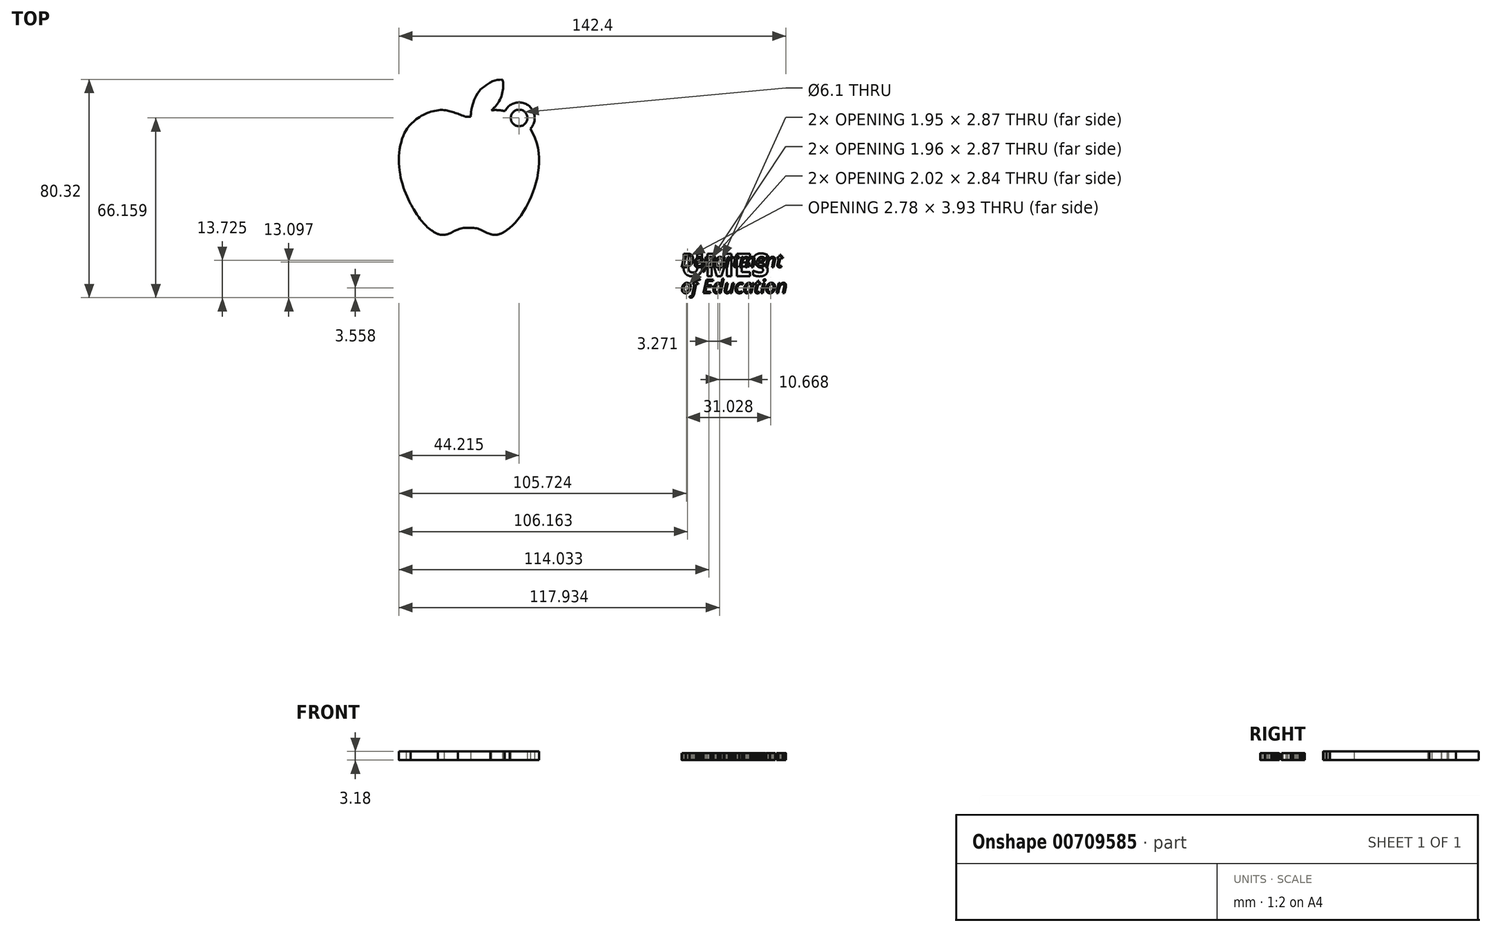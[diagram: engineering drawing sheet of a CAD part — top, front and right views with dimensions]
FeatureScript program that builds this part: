
annotation { "Feature Type Name" : "Feature", "Feature Type Description" : "" }
export const myFeature = defineFeature(function(context is Context, id is Id, definition is map)
    precondition{}
    {
        {
            var Q0;
            Q0=qCreatedBy(makeId("Top.planeOp"),FACE);
            var sketch = newSketch(context, id + "F0", { "sketchPlane" : qUnion([Q0])});
            skCircle(sketch, "E0", {"center": v(-59.53, 49.89) * mm, "radius": 3.05 * mm});
            skArc(sketch, "E1", {"start": v(-55.39, 45.93) * mm, "mid": v(-56.24, 54.59) * mm, "end": v(-64.67, 52.43) * mm});
            skFitSpline(sketch, "E2", {"points": [v(-64.67, 52.43) * mm, v(-69.66, 52.66) * mm, v(-71.93, 51.25) * mm], "startDerivative": vector(-9.59, 1.47) * mm, "endDerivative": vector(-4.68, -4.12) * mm});
            skFitSpline(sketch, "E3", {"points": [v(-69.66, 52.66) * mm, v(-66.9, 56.02) * mm, v(-65.54, 59.96) * mm, v(-65.4, 62.82) * mm, v(-65.72, 64.05) * mm], "startDerivative": vector(10.2, 10.54) * mm, "endDerivative": vector(-2.35, 6.78) * mm});
            skFitSpline(sketch, "E4", {"points": [v(-65.72, 64.05) * mm, v(-68.98, 63.5) * mm, v(-71.84, 61.82) * mm, v(-74.02, 60) * mm, v(-75.65, 57.33) * mm, v(-76.7, 54.52) * mm, v(-77.24, 51.57) * mm, v(-77.33, 50.3) * mm], "startDerivative": vector(-21.52, -1.58) * mm, "endDerivative": vector(-0.5, -11.65) * mm});
            skFitSpline(sketch, "E5", {"points": [v(-55.39, 45.93) * mm, v(-53.32, 41.64) * mm, v(-52.33, 36.83) * mm, v(-52.25, 32.55) * mm, v(-52.86, 27.98) * mm, v(-54.08, 23.47) * mm, v(-55.53, 19.81) * mm, v(-56.76, 17.52) * mm, v(-58.66, 14.32) * mm, v(-61.1, 11.26) * mm, v(-63.03, 9.37) * mm], "startDerivative": vector(20.95, -37.89) * mm, "endDerivative": vector(-22.74, -21.29) * mm});
            skFitSpline(sketch, "E6", {"points": [v(-77.33, 50.3) * mm, v(-78.34, 50.3) * mm, v(-79, 50.3) * mm, v(-80.29, 50.74) * mm, v(-82.2, 51.46) * mm, v(-84.15, 52.11) * mm, v(-86.09, 52.63) * mm, v(-87.15, 52.8) * mm], "startDerivative": vector(-8.93, 0.19) * mm, "endDerivative": vector(-7.8, 1.04) * mm});
            skFitSpline(sketch, "E7", {"points": [v(-101.1, 45.32) * mm, v(-100.2, 46.7) * mm, v(-99.27, 47.73) * mm, v(-98.15, 48.76) * mm, v(-96.8, 49.81) * mm, v(-95.2, 50.8) * mm, v(-93.47, 51.64) * mm, v(-91.57, 52.29) * mm, v(-90.06, 52.6) * mm, v(-88.52, 52.83) * mm, v(-87.15, 52.8) * mm], "startDerivative": vector(8.76, 14.5) * mm, "endDerivative": vector(14.81, -1) * mm});
            skFitSpline(sketch, "E8", {"points": [v(-101.1, 45.32) * mm, v(-101.75, 44.24) * mm, v(-102.36, 42.8) * mm, v(-102.82, 41.3) * mm, v(-103.27, 39.67) * mm, v(-103.54, 37.87) * mm, v(-103.73, 36.2) * mm, v(-103.73, 34.25) * mm, v(-103.73, 32.5) * mm, v(-103.52, 30.7) * mm, v(-103.21, 28.58) * mm, v(-102.83, 26.87) * mm, v(-102.4, 25.42) * mm, v(-102.07, 24.05) * mm, v(-101.5, 22.75) * mm, v(-100.84, 21.22) * mm, v(-100.41, 20.18) * mm, v(-100.06, 19.34) * mm, v(-99.47, 18.24) * mm], "startDerivative": vector(-13.27, -20.53) * mm, "endDerivative": vector(12.8, -22.8) * mm});
            skFitSpline(sketch, "E9", {"points": [v(-99.47, 18.24) * mm, v(-98.54, 16.65) * mm, v(-97.38, 14.75) * mm, v(-96.55, 13.57) * mm, v(-95.62, 12.25) * mm, v(-94.5, 10.97) * mm, v(-93.44, 9.81) * mm, v(-92.44, 8.98) * mm, v(-91.35, 8.2) * mm, v(-90.45, 7.6) * mm, v(-89.4, 7.18) * mm], "startDerivative": vector(8.04, -13.82) * mm, "endDerivative": vector(12.7, -4.22) * mm});
            skFitSpline(sketch, "E10", {"points": [v(-89.4, 7.18) * mm, v(-88.6, 6.95) * mm, v(-87.72, 6.85) * mm, v(-86.76, 6.9) * mm, v(-85.75, 7.18) * mm, v(-84.52, 7.67) * mm, v(-83.34, 8.3) * mm, v(-82.1, 8.85) * mm], "startDerivative": vector(6.26, -2.17) * mm, "endDerivative": vector(8.03, 3.6) * mm});
            skFitSpline(sketch, "E11", {"points": [v(-82.1, 8.85) * mm, v(-81.18, 9.18) * mm, v(-80.27, 9.35) * mm, v(-79.35, 9.42) * mm, v(-78.35, 9.45) * mm, v(-77.1, 9.42) * mm, v(-76.37, 9.42) * mm, v(-75.5, 9.33) * mm, v(-74.67, 9.13) * mm, v(-73.87, 8.85) * mm, v(-73.18, 8.46) * mm, v(-72.14, 7.93) * mm, v(-71.2, 7.52) * mm, v(-70.12, 7.18) * mm], "startDerivative": vector(11.59, 4.14) * mm, "endDerivative": vector(13.32, -3.83) * mm});
            skFitSpline(sketch, "E12", {"points": [v(-70.12, 7.18) * mm, v(-69.26, 6.92) * mm, v(-68.37, 6.9) * mm, v(-67.4, 6.97) * mm, v(-65.97, 7.45) * mm, v(-64.88, 8.05) * mm], "startDerivative": vector(4.7, -1.76) * mm, "endDerivative": vector(4.74, 2.9) * mm});
            skFitSpline(sketch, "E13", {"points": [v(-64.88, 8.05) * mm, v(-64.02, 8.65) * mm, v(-63.03, 9.37) * mm], "startDerivative": vector(1.77, 1.22) * mm, "endDerivative": vector(1.94, 1.42) * mm});
            skSolve(sketch);
        }
        {
            var Q0;
            Q0=qCreatedBy(makeId("Top.planeOp"),FACE);
            var sketch = newSketch(context, id + "F1", { "sketchPlane" : qUnion([Q0])});
            skText(sketch, "E14", { "text": "UMES\n", "fontName": "NotoSans-Bold.ttf"});
            const initialGuessF1  = {"E14": [0, -0.0083, 1, 0, 0.0083]};
            skSetInitialGuess(sketch, initialGuessF1);
            skSolve(sketch);
        }
        {
            var Q0;
            Q0=makeQuery(id+"F0.imprint","IMPRINT",FACE,{"disambiguationData":[TD([[makeQuery(id+"F0.imprint","IMPRINT",EDGE,{"derivedFrom":sQuery(id+"F0.wireOp",EDGE,"E0")}),-1.0]])]});
            extrude(context, id + "F2", {"entities" : qUnion([Q0]), "depth" : 3.17 * mm, "offsetDistance" : 25.4 * mm});
        }
        {
            var Q0;
            Q0 = qSketchRegion(id + "F1", true);
            extrude(context, id + "F3", {"entities" : qUnion([Q0]), "depth" : 2.54 * mm, "offsetDistance" : 25.4 * mm});
        }
        {
            var Q0;
            Q0=qCreatedBy(makeId("Top.planeOp"),FACE);
            var sketch = newSketch(context, id + "F4", { "sketchPlane" : qUnion([Q0])});
            skText(sketch, "E15", { "text": "Department\nof Education", "fontName": "NotoSans-Italic.ttf"});
            const initialGuessF4  = {"E15": [0, -0.00505, 1, 0, 0.00505]};
            skSetInitialGuess(sketch, initialGuessF4);
            skSolve(sketch);
        }
        {
            var Q0;
            Q0 = qSketchRegion(id + "F4", true);
            extrude(context, id + "F5", {"entities" : qUnion([Q0]), "depth" : 2.54 * mm, "offsetDistance" : 25.4 * mm});
        }
    });
